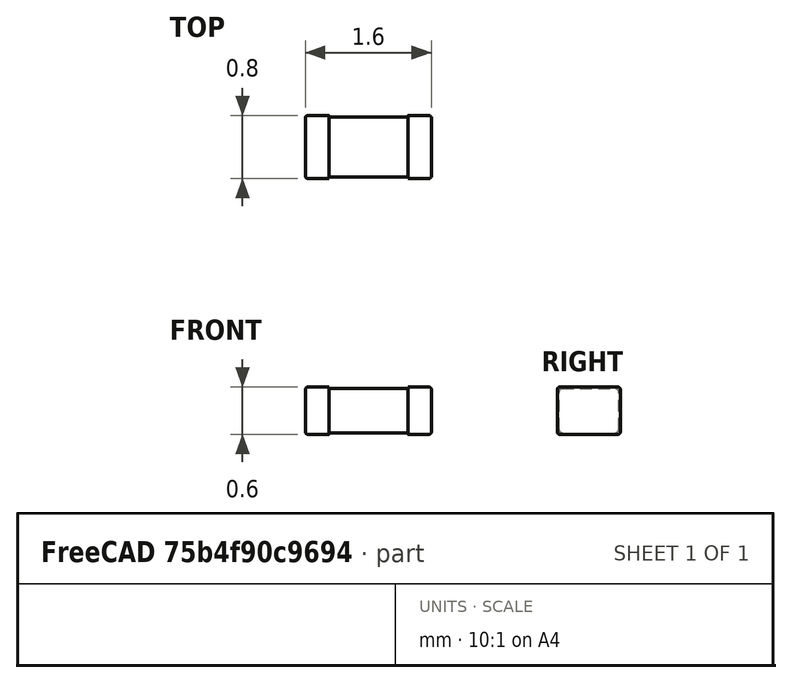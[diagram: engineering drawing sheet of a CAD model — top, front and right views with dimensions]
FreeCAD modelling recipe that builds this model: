
FCSTD DOCUMENT  (FreeCAD 0.16R6703 (Git))
Label: L_0603
License: All rights reserved
LicenseURL: http://en.wikipedia.org/wiki/All_rights_reserved
objects: Part::FeaturePython×4, Part::Box×2, Part::Fillet×2, Part::Mirroring×1, App::DocumentObjectGroup×1
note: 9 computed .brp shape members not serialized (recipe doc carries the construction recipe); baked Part::Feature solids carry a one-line shape summary decoded from their .brp

FEATURE [Part::Box] Box  label="Cube"
  Height = 0.56
  Length = 1
  Placement = pos=(-0.5,-0.38,0.02) rot=(0,0,1;0rad)
  Width = 0.76
FEATURE [Part::Fillet] Fillet  label="body-src"
  Base = -> Box
  Edges = 4 edges r=0.04: [Edge9,Edge10,Edge11,Edge12]
FEATURE [Part::Box] Box001  label="side-src"
  Height = 0.6
  Length = 0.3
  Placement = pos=(-0.8,-0.4,0) rot=(0,0,1;0rad)
  Width = 0.8
FEATURE [Part::Fillet] Fillet001  label="left-side-src"
  Base = -> Box001
  Edges = 8 edges r=0.03: [Edge1,Edge2,Edge3,Edge4,Edge9,Edge10,Edge11,Edge12]
FEATURE [Part::FeaturePython] Clone001  label="left-side-2"  # Draft clone (typed FeaturePython)
  Objects = -> [Fillet001]
  Scale = (1,1,1)
FEATURE [Part::Mirroring] Part__Mirroring  label="right-side-src"
  Base = (0,0,0)
  Normal = (1,0,0)
  Source = -> Clone001
FEATURE [App::DocumentObjectGroup] Group  label="src"
  Group = -> [Fillet,Box001,Fillet001,Part__Mirroring]
FEATURE [Part::FeaturePython] Clone  label="body"  # Draft clone (typed FeaturePython)
  Objects = -> [Fillet]
  Scale = (1,1,1)
FEATURE [Part::FeaturePython] Clone003  label="right-side"  # Draft clone (typed FeaturePython)
  Objects = -> [Part__Mirroring]
  Scale = (1,1,1)
FEATURE [Part::FeaturePython] Clone004  label="left-side"  # Draft clone (typed FeaturePython)
  Objects = -> [Clone001]
  Scale = (1,1,1)
